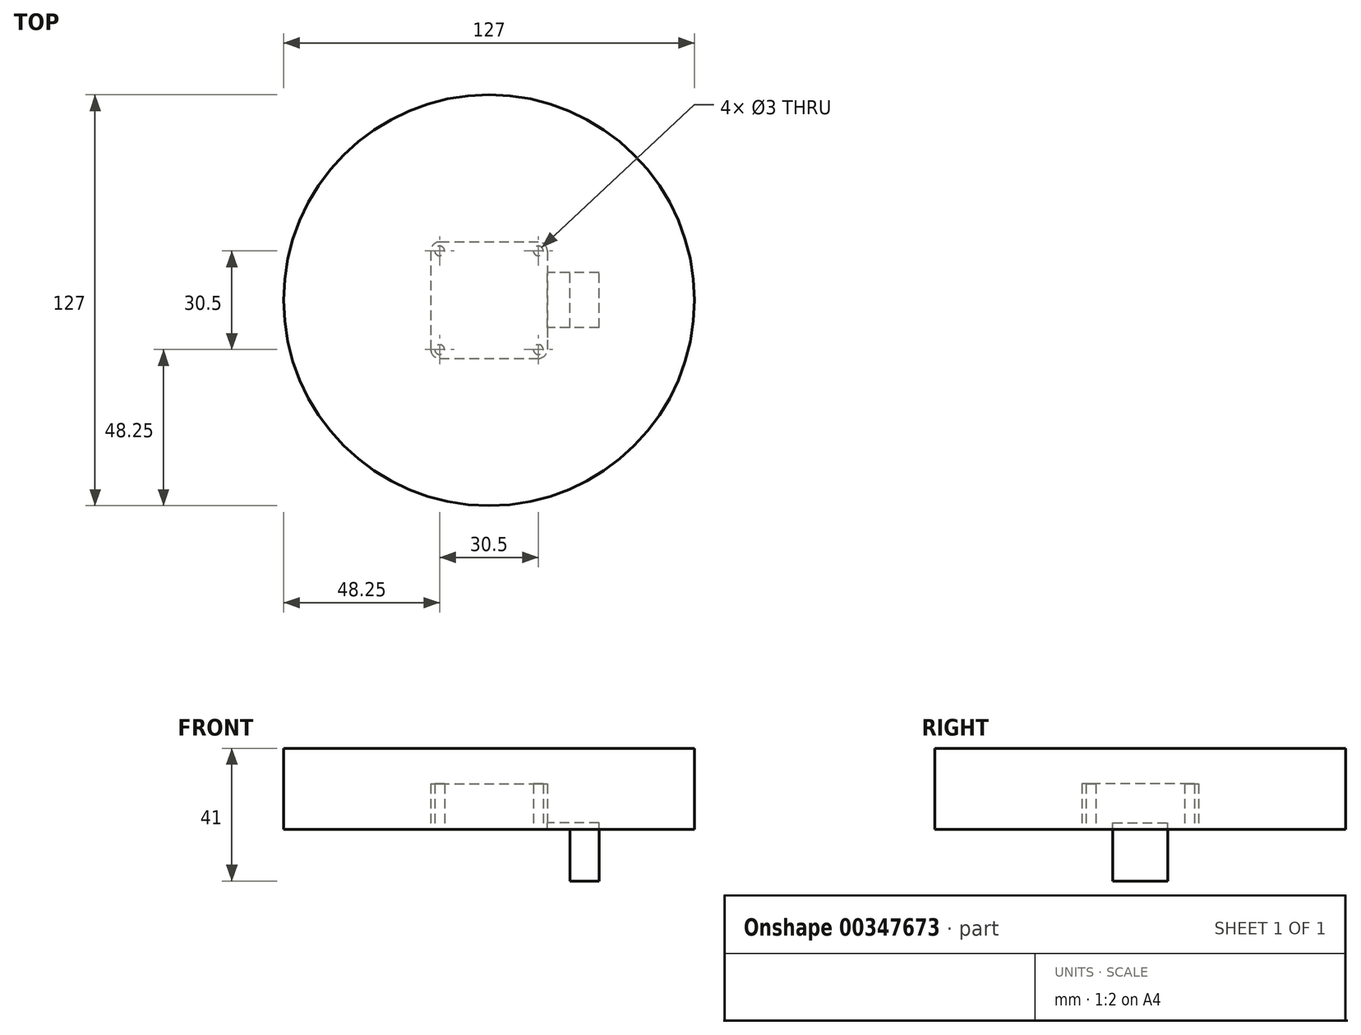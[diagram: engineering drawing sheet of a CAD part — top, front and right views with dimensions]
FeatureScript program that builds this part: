
annotation { "Feature Type Name" : "Feature", "Feature Type Description" : "" }
export const myFeature = defineFeature(function(context is Context, id is Id, definition is map)
    precondition{}
    {
        {
            var Q0;
            Q0=qCreatedBy(makeId("Top.planeOp"),FACE);
            var sketch = newSketch(context, id + "F0", { "sketchPlane" : qUnion([Q0])});
            skLineSegment(sketch, "E0.bottom", {"start": v(-15.25, 18) * mm, "end": v(15.25, 18) * mm});
            skLineSegment(sketch, "E0.top", {"start": v(-15.25, -18) * mm, "end": v(15.25, -18) * mm});
            skLineSegment(sketch, "E0.left", {"start": v(-18, 15.25) * mm, "end": v(-18, -15.25) * mm});
            skLineSegment(sketch, "E0.right", {"start": v(18, 15.25) * mm, "end": v(18, -15.25) * mm});
            skPoint(sketch, "E1.visualSharp", {"position": v(-18, 18) * mm});
            skArc(sketch, "E1.filletArc", {"start": v(-15.25, 18) * mm, "mid": v(-17.2, 17.2) * mm, "end": v(-18, 15.25) * mm});
            skPoint(sketch, "E2.visualSharp", {"position": v(-18, -18) * mm});
            skArc(sketch, "E2.filletArc", {"start": v(-18, -15.25) * mm, "mid": v(-17.2, -17.2) * mm, "end": v(-15.25, -18) * mm});
            skPoint(sketch, "E3.visualSharp", {"position": v(18, -18) * mm});
            skArc(sketch, "E3.filletArc", {"start": v(15.25, -18) * mm, "mid": v(17.2, -17.2) * mm, "end": v(18, -15.25) * mm});
            skPoint(sketch, "E4.visualSharp", {"position": v(18, 18) * mm});
            skArc(sketch, "E4.filletArc", {"start": v(18, 15.25) * mm, "mid": v(17.2, 17.2) * mm, "end": v(15.25, 18) * mm});
            skCircle(sketch, "E5", {"center": v(-15.25, 15.25) * mm, "radius": 1.5 * mm});
            skCircle(sketch, "E6", {"center": v(15.25, 15.25) * mm, "radius": 1.5 * mm});
            skCircle(sketch, "E7", {"center": v(-15.25, -15.25) * mm, "radius": 1.5 * mm});
            skCircle(sketch, "E8", {"center": v(15.25, -15.25) * mm, "radius": 1.5 * mm});
            skSolve(sketch);
        }
        {
            var Q0;
            Q0=makeQuery(id+"F0.imprint","IMPRINT",FACE,{"disambiguationData":[TD([[makeQuery(id+"F0.imprint","IMPRINT",EDGE,{"derivedFrom":sQuery(id+"F0.wireOp",EDGE,"E0.bottom")}),-1.0]])]});
            extrude(context, id + "F1", {"entities" : qUnion([Q0]), "depth" : 14 * mm});
        }
        {
            var Q0;
            Q0=makeQuery(id+"F1.opExtrude","SWEPT_FACE",FACE,{"disambiguationData":[OSD([sQuery(id+"F0.wireOp",EDGE,"E0.right")])]});
            var sketch = newSketch(context, id + "F2", { "sketchPlane" : qUnion([Q0])});
            skLineSegment(sketch, "E9.bottom", {"start": v(-8.5, 0) * mm, "end": v(8.5, 0) * mm});
            skLineSegment(sketch, "E9.top", {"start": v(-8.5, 2) * mm, "end": v(8.5, 2) * mm});
            skLineSegment(sketch, "E9.left", {"start": v(-8.5, 0) * mm, "end": v(-8.5, 2) * mm});
            skLineSegment(sketch, "E9.right", {"start": v(8.5, 0) * mm, "end": v(8.5, 2) * mm});
            skSolve(sketch);
        }
        {
            var Q0;
            Q0 = qSketchRegion(id + "F2", true);
            extrude(context, id + "F3", {"entities" : qUnion([Q0]), "operationType" : NewBodyOperationType.ADD, "depth" : 16 * mm});
        }
        {
            var Q0;
            Q0=makeQuery(id+"F3.boolean.opBoolean","MERGE",FACE,{"derivedFrom":[makeQuery(id+"F1.opExtrude","CAP_FACE",FACE,{"disambiguationData":[OSD([sQuery(id+"F0.wireOp",EDGE,"E0.bottom"),sQuery(id+"F0.wireOp",EDGE,"E0.top"),sQuery(id+"F0.wireOp",EDGE,"E0.left"),sQuery(id+"F0.wireOp",EDGE,"E0.right"),sQuery(id+"F0.wireOp",EDGE,"E1.filletArc"),sQuery(id+"F0.wireOp",EDGE,"E2.filletArc"),sQuery(id+"F0.wireOp",EDGE,"E3.filletArc"),sQuery(id+"F0.wireOp",EDGE,"E4.filletArc"),sQuery(id+"F0.wireOp",EDGE,"E5"),sQuery(id+"F0.wireOp",EDGE,"E6"),sQuery(id+"F0.wireOp",EDGE,"E7"),sQuery(id+"F0.wireOp",EDGE,"E8")])],"isStart":true}),makeQuery(id+"F3.opExtrude","SWEPT_FACE",FACE,{"disambiguationData":[OSD([sQuery(id+"F2.wireOp",EDGE,"E9.bottom")])]})]});
            var sketch = newSketch(context, id + "F4", { "sketchPlane" : qUnion([Q0])});
            skLineSegment(sketch, "E10.bottom", {"start": v(34, 8.5) * mm, "end": v(25, 8.5) * mm});
            skLineSegment(sketch, "E10.top", {"start": v(34, -8.5) * mm, "end": v(25, -8.5) * mm});
            skLineSegment(sketch, "E10.left", {"start": v(34, 8.5) * mm, "end": v(34, -8.5) * mm});
            skLineSegment(sketch, "E10.right", {"start": v(25, 8.5) * mm, "end": v(25, -8.5) * mm});
            skSolve(sketch);
        }
        {
            var Q0;
            Q0=makeQuery(id+"F4.imprint","IMPRINT",FACE,{"disambiguationData":[TD([[makeQuery(id+"F4.imprint","IMPRINT",EDGE,{"derivedFrom":sQuery(id+"F4.wireOp",EDGE,"E10.bottom")}),1.0]])]});
            extrude(context, id + "F5", {"entities" : qUnion([Q0]), "operationType" : NewBodyOperationType.ADD, "depth" : 16 * mm});
        }
        {
            var Q0;
            Q0=qCreatedBy(makeId("Top.planeOp"),FACE);
            var sketch = newSketch(context, id + "F6", { "sketchPlane" : qUnion([Q0])});
            skCircle(sketch, "E11", {"center": v(0, 0) * mm, "radius": 63.5 * mm});
            skSolve(sketch);
        }
        {
            var Q0;
            Q0=makeQuery(id+"F6.imprint","IMPRINT",FACE,{"disambiguationData":[TD([[makeQuery(id+"F6.imprint","IMPRINT",EDGE,{"derivedFrom":sQuery(id+"F6.wireOp",EDGE,"E11")}),1.0]])]});
            extrude(context, id + "F7", {"entities" : qUnion([Q0]), "depth" : 25 * mm});
        }
    });
